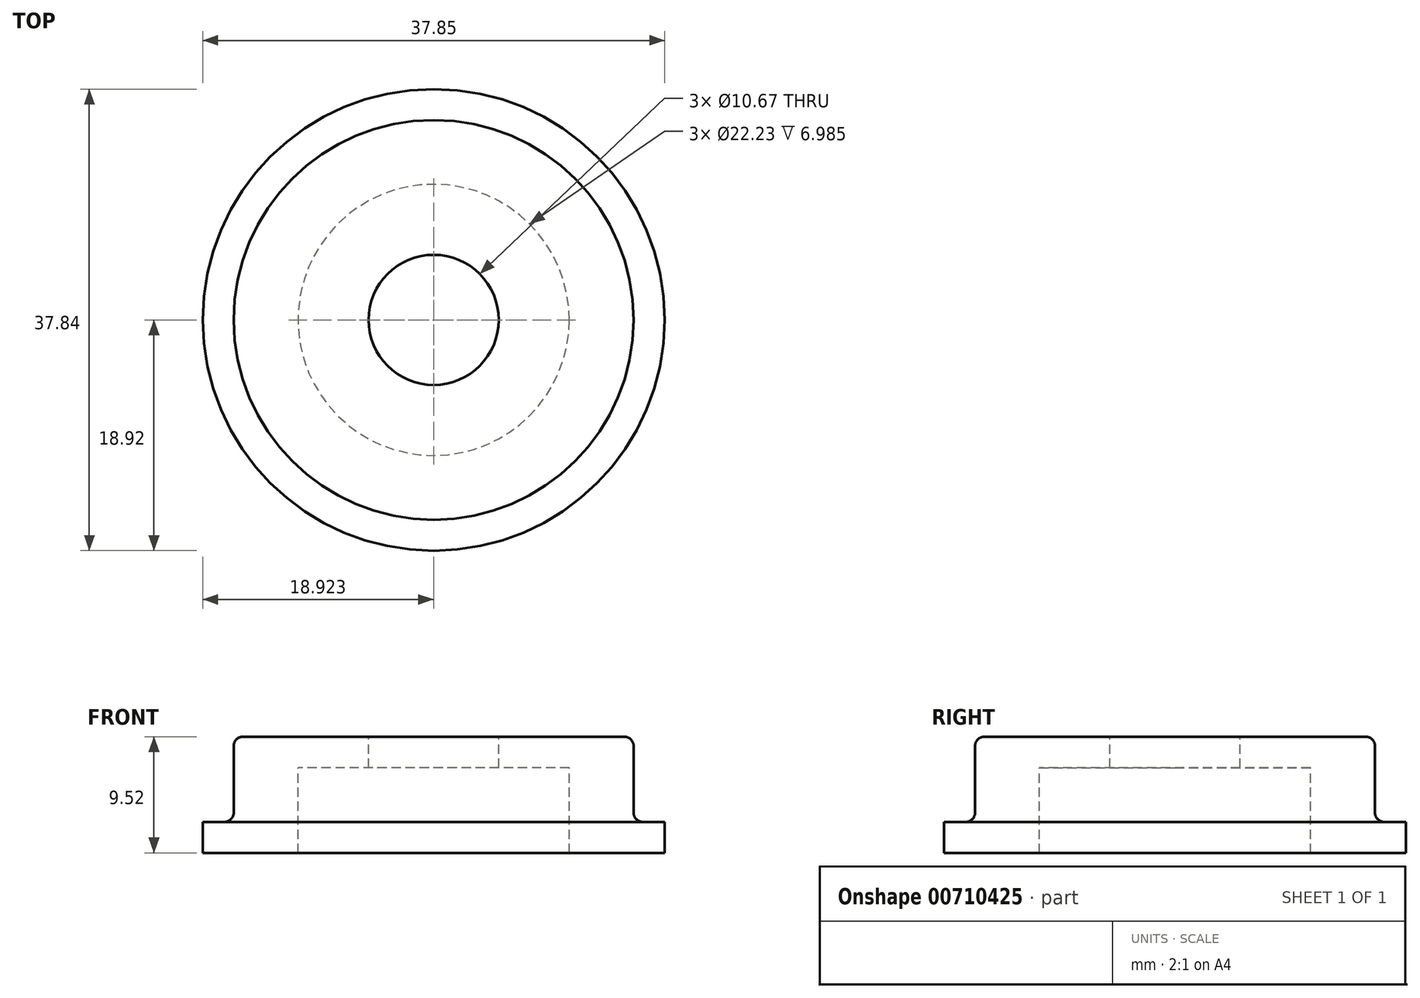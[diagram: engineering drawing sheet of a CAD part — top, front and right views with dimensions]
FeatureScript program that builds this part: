
annotation { "Feature Type Name" : "Feature", "Feature Type Description" : "" }
export const myFeature = defineFeature(function(context is Context, id is Id, definition is map)
    precondition{}
    {
        {
            var Q0;
            Q0=qCreatedBy(makeId("Front.planeOp"),FACE);
            var sketch = newSketch(context, id + "F0", { "sketchPlane" : qUnion([Q0])});
            skLineSegment(sketch, "E0", {"start": v(-44.76, 8.48) * mm, "end": v(-33.64, 8.48) * mm});
            skLineSegment(sketch, "E1", {"start": v(-33.64, 8.48) * mm, "end": v(-33.64, 1.5) * mm});
            skLineSegment(sketch, "E2", {"start": v(-33.64, 1.5) * mm, "end": v(-25.83, 1.5) * mm});
            skLineSegment(sketch, "E3", {"start": v(-25.83, 1.5) * mm, "end": v(-25.83, 4.04) * mm});
            skLineSegment(sketch, "E4", {"start": v(-25.83, 4.04) * mm, "end": v(-28.37, 4.04) * mm});
            skLineSegment(sketch, "E5", {"start": v(-28.37, 4.04) * mm, "end": v(-28.37, 11.02) * mm});
            skLineSegment(sketch, "E6", {"start": v(-28.37, 11.02) * mm, "end": v(-44.76, 11.02) * mm});
            skLineSegment(sketch, "E7", {"start": v(-44.76, 11.02) * mm, "end": v(-44.76, 8.48) * mm});
            skLineSegment(sketch, "E8", {"start": v(-39.42, 11.02) * mm, "end": v(-39.42, 8.48) * mm});
            skLineSegment(sketch, "E9", {"start": v(-44.76, 11.02) * mm, "end": v(-44.76, -5.08) * mm});
            skSolve(sketch);
        }
        {
            var Q0;
            {var subQ0=sQuery(id+"F0.wireOp",EDGE,"E1");Q0=makeQuery(id+"F0.imprint","IMPRINT",FACE,{"disambiguationData":[TD([[makeQuery(id+"F0.imprint","IMPRINT",EDGE,{"derivedFrom":subQ0}),1.0]])]});}
            var Q1;
            Q1=sQuery(id+"F0.wireOp",EDGE,"E9");
            revolve(context, id + "F1", {"surfaceOperationType" : NewSurfaceOperationType.NEW, "entities" : qUnion([Q0]), "axis" : qUnion([Q1]), "revolveType" : RevolveType.FULL});
        }
        {
            var Q0;
            Q0=makeQuery(id+"F1.opRevolve","SWEPT_EDGE",EDGE,{"disambiguationData":[OSD([sQuery(id+"F0.wireOp",EDGE,"E5"),sQuery(id+"F0.wireOp",EDGE,"E6")])]});
            var Q1;
            Q1=makeQuery(id+"F1.opRevolve","SWEPT_FACE",FACE,{"disambiguationData":[OSD([sQuery(id+"F0.wireOp",EDGE,"E5")])]});
            fillet(context, id + "F2", {"entities" : qUnion([Q0, Q1]), "radius" : 0.76 * mm, "tangentPropagation" : true, "allowEdgeOverflow" : false});
        }
    });
